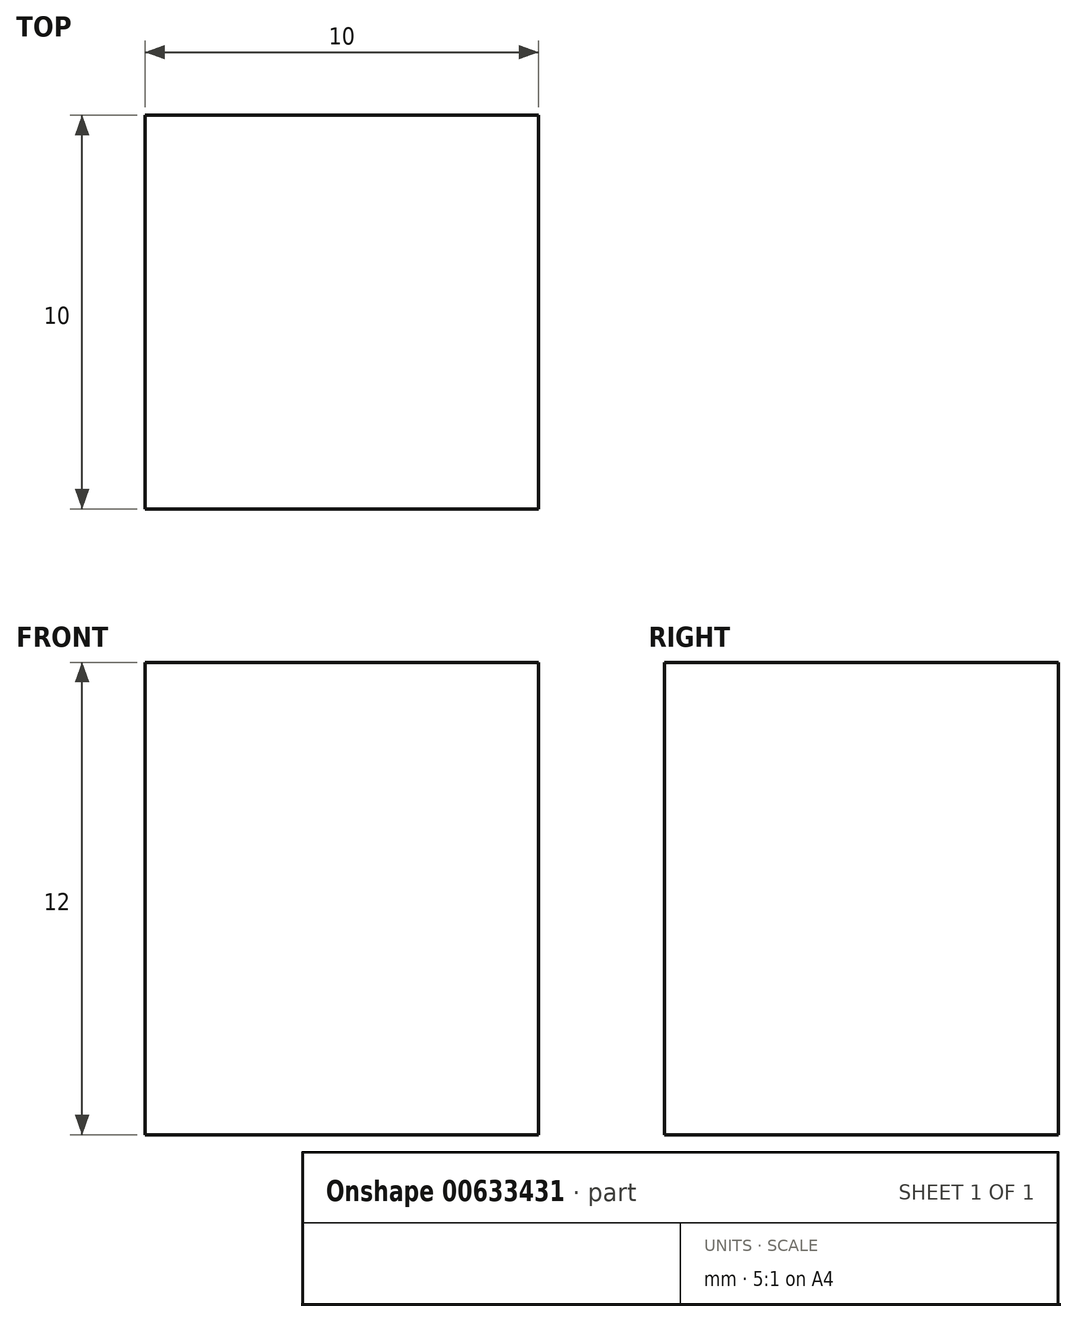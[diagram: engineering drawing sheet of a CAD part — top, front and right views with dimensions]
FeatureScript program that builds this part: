
annotation { "Feature Type Name" : "Feature", "Feature Type Description" : "" }
export const myFeature = defineFeature(function(context is Context, id is Id, definition is map)
    precondition{}
    {
        {
            var Q0;
            Q0=qCreatedBy(makeId("Top.planeOp"),FACE);
            var sketch = newSketch(context, id + "F0", { "sketchPlane" : qUnion([Q0])});
            skLineSegment(sketch, "E0.bottom", {"start": v(0, 0) * mm, "end": v(10, 0) * mm});
            skLineSegment(sketch, "E0.top", {"start": v(0, 10) * mm, "end": v(10, 10) * mm});
            skLineSegment(sketch, "E0.left", {"start": v(0, 0) * mm, "end": v(0, 10) * mm});
            skLineSegment(sketch, "E0.right", {"start": v(10, 0) * mm, "end": v(10, 10) * mm});
            skSolve(sketch);
        }
        {
            var Q0;
            Q0=makeQuery(id+"F0.imprint","IMPRINT",FACE,{"disambiguationData":[TD([[makeQuery(id+"F0.imprint","IMPRINT",EDGE,{"derivedFrom":sQuery(id+"F0.wireOp",EDGE,"E0.bottom")}),1.0]])]});
            extrude(context, id + "F1", {"entities" : qUnion([Q0]), "depth" : 12 * mm, "offsetDistance" : 25 * mm});
        }
    });
